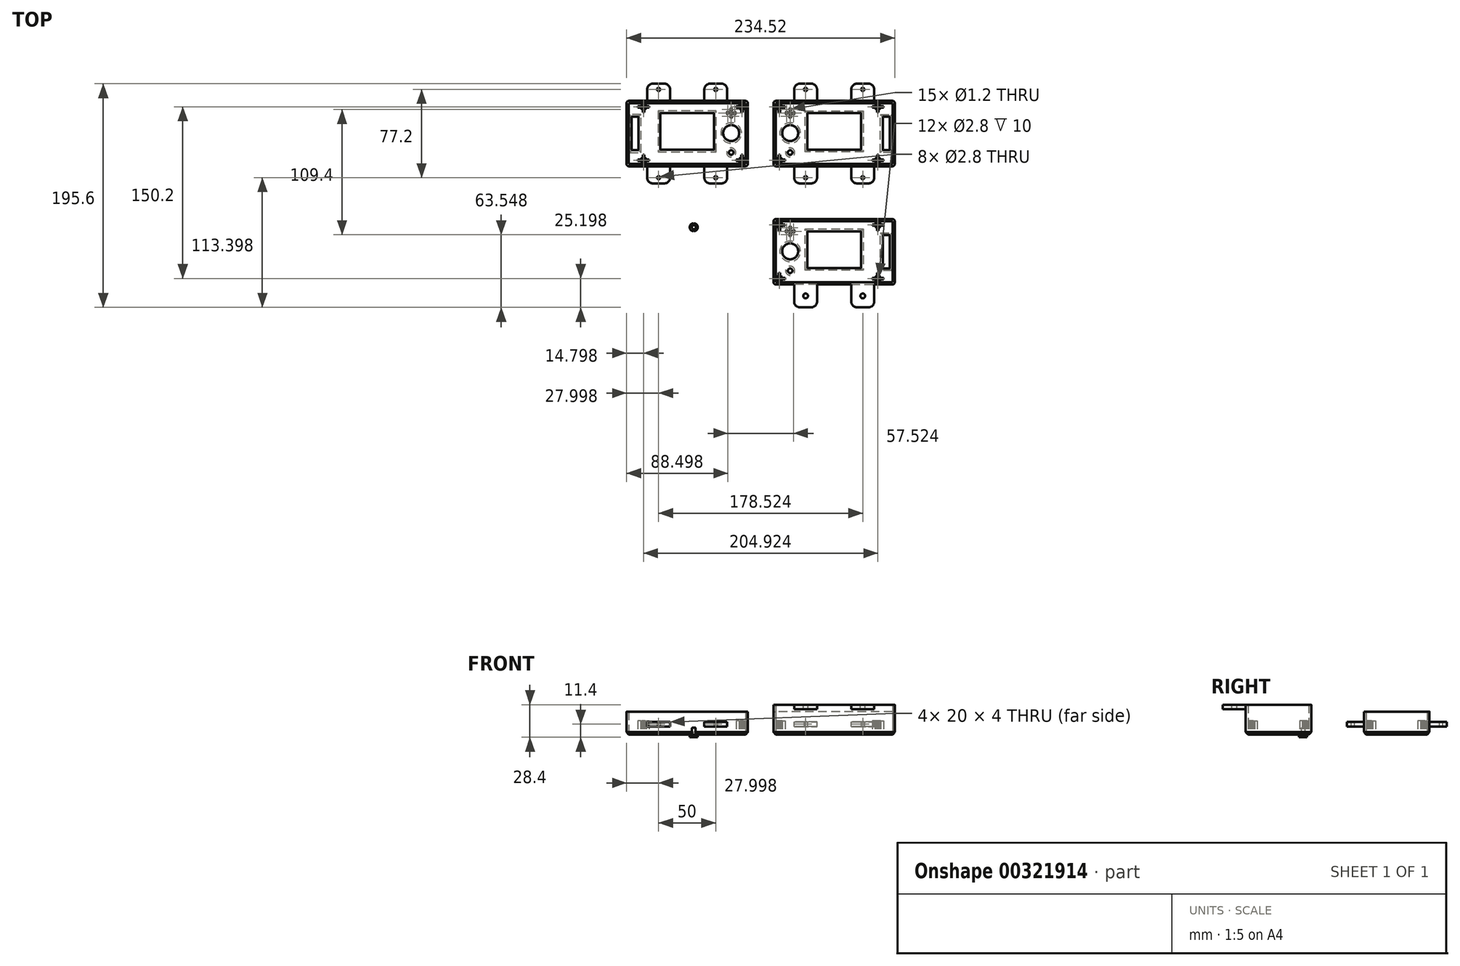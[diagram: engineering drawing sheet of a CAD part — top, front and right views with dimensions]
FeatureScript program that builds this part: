
annotation { "Feature Type Name" : "Feature", "Feature Type Description" : "" }
export const myFeature = defineFeature(function(context is Context, id is Id, definition is map)
    precondition{}
    {
        {
            var Q0;
            Q0=qCreatedBy(makeId("Top.planeOp"),FACE);
            var sketch = newSketch(context, id + "F0", { "sketchPlane" : qUnion([Q0])});
            skLineSegment(sketch, "E0.bottom", {"start": v(-115.26, 57.83) * mm, "end": v(-13.26, 57.83) * mm});
            skLineSegment(sketch, "E0.top", {"start": v(-115.26, 4.63) * mm, "end": v(-13.26, 4.63) * mm});
            skLineSegment(sketch, "E0.left", {"start": v(-115.26, 57.83) * mm, "end": v(-115.26, 4.63) * mm});
            skLineSegment(sketch, "E0.right", {"start": v(-13.26, 57.83) * mm, "end": v(-13.26, 4.63) * mm});
            skLineSegment(sketch, "E1.bottom", {"start": v(-117.26, 59.83) * mm, "end": v(-11.26, 59.83) * mm});
            skLineSegment(sketch, "E1.top", {"start": v(-117.26, 2.63) * mm, "end": v(-11.26, 2.63) * mm});
            skLineSegment(sketch, "E1.left", {"start": v(-117.26, 59.83) * mm, "end": v(-117.26, 2.63) * mm});
            skLineSegment(sketch, "E1.right", {"start": v(-11.26, 59.83) * mm, "end": v(-11.26, 2.63) * mm});
            skLineSegment(sketch, "E2.bottom", {"start": v(-87.76, 49.13) * mm, "end": v(-40.76, 49.13) * mm});
            skLineSegment(sketch, "E2.top", {"start": v(-87.76, 17.13) * mm, "end": v(-40.76, 17.13) * mm});
            skLineSegment(sketch, "E2.left", {"start": v(-87.76, 49.13) * mm, "end": v(-87.76, 17.13) * mm});
            skLineSegment(sketch, "E2.right", {"start": v(-40.76, 49.13) * mm, "end": v(-40.76, 17.13) * mm});
            skCircle(sketch, "E3", {"center": v(-25.76, 31.63) * mm, "radius": 7 * mm});
            skCircle(sketch, "E4", {"center": v(-25.76, 14.63) * mm, "radius": 2 * mm});
            skLineSegment(sketch, "E5.bottom", {"start": v(-112.76, 45.83) * mm, "end": v(-106.76, 45.83) * mm});
            skLineSegment(sketch, "E5.top", {"start": v(-112.76, 16.63) * mm, "end": v(-106.76, 16.63) * mm});
            skLineSegment(sketch, "E5.left", {"start": v(-112.76, 45.83) * mm, "end": v(-112.76, 16.63) * mm});
            skLineSegment(sketch, "E5.right", {"start": v(-106.76, 45.83) * mm, "end": v(-106.76, 16.63) * mm});
            skCircle(sketch, "E6", {"center": v(-25.76, 49.18) * mm, "radius": 0.6 * mm});
            skCircle(sketch, "E7", {"center": v(-28.76, 49.18) * mm, "radius": 0.6 * mm});
            skCircle(sketch, "E8", {"center": v(-25.76, 46.18) * mm, "radius": 0.6 * mm});
            skCircle(sketch, "E9", {"center": v(-22.76, 49.18) * mm, "radius": 0.6 * mm});
            skCircle(sketch, "E10", {"center": v(-25.76, 52.18) * mm, "radius": 0.6 * mm});
            skSolve(sketch);
        }
        {
            var Q0;
            Q0=makeQuery(id+"F0.imprint","IMPRINT",FACE,{"disambiguationData":[TD([[makeQuery(id+"F0.imprint","IMPRINT",EDGE,{"derivedFrom":sQuery(id+"F0.wireOp",EDGE,"E0.bottom")}),-1.0]])]});
            extrude(context, id + "F1", {"entities" : qUnion([Q0]), "depth" : 2 * mm, "offsetDistance" : 25 * mm});
        }
        {
            var Q0;
            Q0=makeQuery(id+"F0.imprint","IMPRINT",FACE,{"disambiguationData":[TD([[makeQuery(id+"F0.imprint","IMPRINT",EDGE,{"derivedFrom":sQuery(id+"F0.wireOp",EDGE,"E0.bottom")}),1.0]])]});
            extrude(context, id + "F2", {"entities" : qUnion([Q0]), "operationType" : NewBodyOperationType.ADD, "depth" : 20 * mm, "offsetDistance" : 25 * mm});
        }
        {
            var Q0;
            Q0=makeQuery(id+"F1.opExtrude","CAP_FACE",FACE,{"disambiguationData":[OSD([sQuery(id+"F0.wireOp",EDGE,"E0.bottom"),sQuery(id+"F0.wireOp",EDGE,"E0.top"),sQuery(id+"F0.wireOp",EDGE,"E0.left"),sQuery(id+"F0.wireOp",EDGE,"E0.right"),sQuery(id+"F0.wireOp",EDGE,"E2.bottom"),sQuery(id+"F0.wireOp",EDGE,"E2.top"),sQuery(id+"F0.wireOp",EDGE,"E2.left"),sQuery(id+"F0.wireOp",EDGE,"E2.right"),sQuery(id+"F0.wireOp",EDGE,"E3"),sQuery(id+"F0.wireOp",EDGE,"E4")])],"isStart":false});
            var sketch = newSketch(context, id + "F3", { "sketchPlane" : qUnion([Q0])});
            skCircle(sketch, "E11", {"center": v(-16.46, 54.63) * mm, "radius": 1.4 * mm});
            skCircle(sketch, "E12", {"center": v(-16.46, 7.83) * mm, "radius": 1.4 * mm});
            skCircle(sketch, "E13", {"center": v(-102.46, 54.63) * mm, "radius": 1.4 * mm});
            skCircle(sketch, "E14", {"center": v(-102.46, 7.83) * mm, "radius": 1.4 * mm});
            skCircle(sketch, "E15", {"center": v(-16.46, 54.63) * mm, "radius": 2.6 * mm});
            skCircle(sketch, "E16", {"center": v(-16.46, 7.83) * mm, "radius": 2.6 * mm});
            skCircle(sketch, "E17", {"center": v(-102.46, 7.83) * mm, "radius": 2.6 * mm});
            skCircle(sketch, "E18", {"center": v(-102.46, 54.63) * mm, "radius": 2.6 * mm});
            skLineSegment(sketch, "E19.top", {"start": v(-17.06, 49.7) * mm, "end": v(-15.86, 49.7) * mm});
            skLineSegment(sketch, "E19.left", {"start": v(-17.06, 52.1) * mm, "end": v(-17.06, 49.7) * mm});
            skLineSegment(sketch, "E19.right", {"start": v(-15.86, 52.1) * mm, "end": v(-15.86, 49.7) * mm});
            skLineSegment(sketch, "E20.bottom", {"start": v(-19, 55.23) * mm, "end": v(-21.4, 55.23) * mm});
            skLineSegment(sketch, "E20.top", {"start": v(-19, 54.03) * mm, "end": v(-21.4, 54.03) * mm});
            skLineSegment(sketch, "E20.right", {"start": v(-21.4, 55.23) * mm, "end": v(-21.4, 54.03) * mm});
            skLineSegment(sketch, "E21.top", {"start": v(-17.06, 57.83) * mm, "end": v(-15.86, 57.83) * mm});
            skLineSegment(sketch, "E21.left", {"start": v(-17.06, 57.16) * mm, "end": v(-17.06, 57.83) * mm});
            skLineSegment(sketch, "E21.right", {"start": v(-15.86, 57.16) * mm, "end": v(-15.86, 57.83) * mm});
            skLineSegment(sketch, "E22.bottom", {"start": v(-13.93, 55.23) * mm, "end": v(-13.26, 55.23) * mm});
            skLineSegment(sketch, "E22.top", {"start": v(-13.93, 54.03) * mm, "end": v(-13.26, 54.03) * mm});
            skLineSegment(sketch, "E22.right", {"start": v(-13.26, 55.23) * mm, "end": v(-13.26, 54.03) * mm});
            skLineSegment(sketch, "E23.top", {"start": v(-17.06, 12.76) * mm, "end": v(-15.86, 12.76) * mm});
            skLineSegment(sketch, "E23.left", {"start": v(-17.06, 10.36) * mm, "end": v(-17.06, 12.76) * mm});
            skLineSegment(sketch, "E23.right", {"start": v(-15.86, 10.36) * mm, "end": v(-15.86, 12.76) * mm});
            skLineSegment(sketch, "E24.bottom", {"start": v(-19, 8.43) * mm, "end": v(-21.4, 8.43) * mm});
            skLineSegment(sketch, "E24.top", {"start": v(-19, 7.23) * mm, "end": v(-21.4, 7.23) * mm});
            skLineSegment(sketch, "E24.right", {"start": v(-21.4, 8.43) * mm, "end": v(-21.4, 7.23) * mm});
            skLineSegment(sketch, "E25.top", {"start": v(-17.06, 4.63) * mm, "end": v(-15.86, 4.63) * mm});
            skLineSegment(sketch, "E25.left", {"start": v(-17.06, 5.3) * mm, "end": v(-17.06, 4.63) * mm});
            skLineSegment(sketch, "E25.right", {"start": v(-15.86, 5.3) * mm, "end": v(-15.86, 4.63) * mm});
            skLineSegment(sketch, "E26.bottom", {"start": v(-13.93, 7.23) * mm, "end": v(-13.26, 7.23) * mm});
            skLineSegment(sketch, "E26.top", {"start": v(-13.93, 8.43) * mm, "end": v(-13.26, 8.43) * mm});
            skLineSegment(sketch, "E26.right", {"start": v(-13.26, 7.23) * mm, "end": v(-13.26, 8.43) * mm});
            skLineSegment(sketch, "E27.bottom", {"start": v(-105, 55.23) * mm, "end": v(-107.4, 55.23) * mm});
            skLineSegment(sketch, "E27.top", {"start": v(-105, 54.03) * mm, "end": v(-107.4, 54.03) * mm});
            skLineSegment(sketch, "E27.right", {"start": v(-107.4, 55.23) * mm, "end": v(-107.4, 54.03) * mm});
            skLineSegment(sketch, "E28.bottom", {"start": v(-99.93, 55.23) * mm, "end": v(-97.53, 55.23) * mm});
            skLineSegment(sketch, "E28.top", {"start": v(-99.93, 54.03) * mm, "end": v(-97.53, 54.03) * mm});
            skLineSegment(sketch, "E28.right", {"start": v(-97.53, 55.23) * mm, "end": v(-97.53, 54.03) * mm});
            skLineSegment(sketch, "E29.top", {"start": v(-103.06, 49.7) * mm, "end": v(-101.86, 49.7) * mm});
            skLineSegment(sketch, "E29.left", {"start": v(-103.06, 52.1) * mm, "end": v(-103.06, 49.7) * mm});
            skLineSegment(sketch, "E29.right", {"start": v(-101.86, 52.1) * mm, "end": v(-101.86, 49.7) * mm});
            skLineSegment(sketch, "E30.top", {"start": v(-103.06, 57.83) * mm, "end": v(-101.86, 57.83) * mm});
            skLineSegment(sketch, "E30.left", {"start": v(-103.06, 57.16) * mm, "end": v(-103.06, 57.83) * mm});
            skLineSegment(sketch, "E30.right", {"start": v(-101.86, 57.16) * mm, "end": v(-101.86, 57.83) * mm});
            skLineSegment(sketch, "E31.top", {"start": v(-103.06, 12.76) * mm, "end": v(-101.86, 12.76) * mm});
            skLineSegment(sketch, "E31.left", {"start": v(-103.06, 10.36) * mm, "end": v(-103.06, 12.76) * mm});
            skLineSegment(sketch, "E31.right", {"start": v(-101.86, 10.36) * mm, "end": v(-101.86, 12.76) * mm});
            skLineSegment(sketch, "E32.bottom", {"start": v(-105, 8.43) * mm, "end": v(-107.4, 8.43) * mm});
            skLineSegment(sketch, "E32.top", {"start": v(-105, 7.23) * mm, "end": v(-107.4, 7.23) * mm});
            skLineSegment(sketch, "E32.right", {"start": v(-107.4, 8.43) * mm, "end": v(-107.4, 7.23) * mm});
            skLineSegment(sketch, "E33.bottom", {"start": v(-99.93, 8.43) * mm, "end": v(-97.53, 8.43) * mm});
            skLineSegment(sketch, "E33.top", {"start": v(-99.93, 7.23) * mm, "end": v(-97.53, 7.23) * mm});
            skLineSegment(sketch, "E33.right", {"start": v(-97.53, 8.43) * mm, "end": v(-97.53, 7.23) * mm});
            skLineSegment(sketch, "E34.top", {"start": v(-103.06, 4.63) * mm, "end": v(-101.86, 4.63) * mm});
            skLineSegment(sketch, "E34.left", {"start": v(-103.06, 5.3) * mm, "end": v(-103.06, 4.63) * mm});
            skLineSegment(sketch, "E34.right", {"start": v(-101.86, 5.3) * mm, "end": v(-101.86, 4.63) * mm});
            skLineSegment(sketch, "E35.bottom", {"start": v(-88.96, 50.33) * mm, "end": v(-39.56, 50.33) * mm});
            skLineSegment(sketch, "E35.top", {"start": v(-88.96, 15.93) * mm, "end": v(-39.56, 15.93) * mm});
            skLineSegment(sketch, "E35.left", {"start": v(-88.96, 50.33) * mm, "end": v(-88.96, 15.93) * mm});
            skLineSegment(sketch, "E35.right", {"start": v(-39.56, 50.33) * mm, "end": v(-39.56, 15.93) * mm});
            skSolve(sketch);
        }
        {
            var Q0;
            Q0=makeQuery(id+"F3.imprint","IMPRINT",FACE,{"disambiguationData":[TD([[makeQuery(id+"F3.imprint","IMPRINT",EDGE,{"derivedFrom":sQuery(id+"F3.wireOp",EDGE,"E14")}),-1.0]])]});
            var Q1;
            Q1=makeQuery(id+"F3.imprint","IMPRINT",FACE,{"disambiguationData":[TD([[makeQuery(id+"F3.imprint","IMPRINT",EDGE,{"derivedFrom":sQuery(id+"F3.wireOp",EDGE,"E31.top")}),-1.0]])]});
            var Q2;
            {var subQ0=sQuery(id+"F3.wireOp",EDGE,"E32.bottom");Q2=makeQuery(id+"F3.imprint","IMPRINT",FACE,{"disambiguationData":[TD([[makeQuery(id+"F3.imprint","IMPRINT",EDGE,{"derivedFrom":subQ0}),1.0]])]});}
            var Q3;
            Q3=makeQuery(id+"F3.imprint","IMPRINT",FACE,{"disambiguationData":[TD([[makeQuery(id+"F3.imprint","IMPRINT",EDGE,{"derivedFrom":sQuery(id+"F3.wireOp",EDGE,"E34.top")}),1.0]])]});
            var Q4;
            {var subQ0=sQuery(id+"F3.wireOp",EDGE,"E33.bottom");Q4=makeQuery(id+"F3.imprint","IMPRINT",FACE,{"disambiguationData":[TD([[makeQuery(id+"F3.imprint","IMPRINT",EDGE,{"derivedFrom":subQ0}),-1.0]])]});}
            var Q5;
            {var subQ0=sQuery(id+"F3.wireOp",EDGE,"E24.bottom");Q5=makeQuery(id+"F3.imprint","IMPRINT",FACE,{"disambiguationData":[TD([[makeQuery(id+"F3.imprint","IMPRINT",EDGE,{"derivedFrom":subQ0}),1.0]])]});}
            var Q6;
            Q6=makeQuery(id+"F3.imprint","IMPRINT",FACE,{"disambiguationData":[TD([[makeQuery(id+"F3.imprint","IMPRINT",EDGE,{"derivedFrom":sQuery(id+"F3.wireOp",EDGE,"E12")}),-1.0]])]});
            var Q7;
            Q7=makeQuery(id+"F3.imprint","IMPRINT",FACE,{"disambiguationData":[TD([[makeQuery(id+"F3.imprint","IMPRINT",EDGE,{"derivedFrom":sQuery(id+"F3.wireOp",EDGE,"E25.top")}),1.0]])]});
            var Q8;
            {var subQ0=sQuery(id+"F3.wireOp",EDGE,"E26.bottom");Q8=makeQuery(id+"F3.imprint","IMPRINT",FACE,{"disambiguationData":[TD([[makeQuery(id+"F3.imprint","IMPRINT",EDGE,{"derivedFrom":subQ0}),1.0]])]});}
            var Q9;
            Q9=makeQuery(id+"F3.imprint","IMPRINT",FACE,{"disambiguationData":[TD([[makeQuery(id+"F3.imprint","IMPRINT",EDGE,{"derivedFrom":sQuery(id+"F3.wireOp",EDGE,"E23.top")}),-1.0]])]});
            var Q10;
            Q10=makeQuery(id+"F3.imprint","IMPRINT",FACE,{"disambiguationData":[TD([[makeQuery(id+"F3.imprint","IMPRINT",EDGE,{"derivedFrom":sQuery(id+"F3.wireOp",EDGE,"E11")}),-1.0]])]});
            var Q11;
            {var subQ0=sQuery(id+"F3.wireOp",EDGE,"E22.bottom");Q11=makeQuery(id+"F3.imprint","IMPRINT",FACE,{"disambiguationData":[TD([[makeQuery(id+"F3.imprint","IMPRINT",EDGE,{"derivedFrom":subQ0}),-1.0]])]});}
            var Q12;
            Q12=makeQuery(id+"F3.imprint","IMPRINT",FACE,{"disambiguationData":[TD([[makeQuery(id+"F3.imprint","IMPRINT",EDGE,{"derivedFrom":sQuery(id+"F3.wireOp",EDGE,"E21.top")}),-1.0]])]});
            var Q13;
            {var subQ0=sQuery(id+"F3.wireOp",EDGE,"E20.bottom");Q13=makeQuery(id+"F3.imprint","IMPRINT",FACE,{"disambiguationData":[TD([[makeQuery(id+"F3.imprint","IMPRINT",EDGE,{"derivedFrom":subQ0}),1.0]])]});}
            var Q14;
            Q14=makeQuery(id+"F3.imprint","IMPRINT",FACE,{"disambiguationData":[TD([[makeQuery(id+"F3.imprint","IMPRINT",EDGE,{"derivedFrom":sQuery(id+"F3.wireOp",EDGE,"E19.top")}),1.0]])]});
            var Q15;
            Q15=makeQuery(id+"F3.imprint","IMPRINT",FACE,{"disambiguationData":[TD([[makeQuery(id+"F3.imprint","IMPRINT",EDGE,{"derivedFrom":sQuery(id+"F3.wireOp",EDGE,"E13")}),-1.0]])]});
            var Q16;
            {var subQ0=sQuery(id+"F3.wireOp",EDGE,"E27.bottom");Q16=makeQuery(id+"F3.imprint","IMPRINT",FACE,{"disambiguationData":[TD([[makeQuery(id+"F3.imprint","IMPRINT",EDGE,{"derivedFrom":subQ0}),1.0]])]});}
            var Q17;
            Q17=makeQuery(id+"F3.imprint","IMPRINT",FACE,{"disambiguationData":[TD([[makeQuery(id+"F3.imprint","IMPRINT",EDGE,{"derivedFrom":sQuery(id+"F3.wireOp",EDGE,"E29.top")}),1.0]])]});
            var Q18;
            {var subQ0=sQuery(id+"F3.wireOp",EDGE,"E28.bottom");Q18=makeQuery(id+"F3.imprint","IMPRINT",FACE,{"disambiguationData":[TD([[makeQuery(id+"F3.imprint","IMPRINT",EDGE,{"derivedFrom":subQ0}),-1.0]])]});}
            var Q19;
            Q19=makeQuery(id+"F3.imprint","IMPRINT",FACE,{"disambiguationData":[TD([[makeQuery(id+"F3.imprint","IMPRINT",EDGE,{"derivedFrom":sQuery(id+"F3.wireOp",EDGE,"E30.top")}),-1.0]])]});
            extrude(context, id + "F4", {"entities" : qUnion([Q0, Q1, Q2, Q3, Q4, Q5, Q6, Q7, Q8, Q9, Q10, Q11, Q12, Q13, Q14, Q15, Q16, Q17, Q18, Q19]), "operationType" : NewBodyOperationType.ADD, "depth" : 10 * mm, "offsetDistance" : 25 * mm});
        }
        {
            var Q0;
            Q0=makeQuery(id+"F2.opExtrude","SWEPT_EDGE",EDGE,{"disambiguationData":[OSD([sQuery(id+"F0.wireOp",EDGE,"E1.bottom"),sQuery(id+"F0.wireOp",EDGE,"E1.left")])]});
            var Q1;
            Q1=makeQuery(id+"F2.opExtrude","SWEPT_EDGE",EDGE,{"disambiguationData":[OSD([sQuery(id+"F0.wireOp",EDGE,"E1.top"),sQuery(id+"F0.wireOp",EDGE,"E1.left")])]});
            var Q2;
            Q2=makeQuery(id+"F2.opExtrude","SWEPT_EDGE",EDGE,{"disambiguationData":[OSD([sQuery(id+"F0.wireOp",EDGE,"E1.bottom"),sQuery(id+"F0.wireOp",EDGE,"E1.right")])]});
            var Q3;
            Q3=makeQuery(id+"F2.opExtrude","SWEPT_EDGE",EDGE,{"disambiguationData":[OSD([sQuery(id+"F0.wireOp",EDGE,"E1.top"),sQuery(id+"F0.wireOp",EDGE,"E1.right")])]});
            fillet(context, id + "F5", {"entities" : qUnion([Q0, Q1, Q2, Q3]), "radius" : 2 * mm, "tangentPropagation" : true, "allowEdgeOverflow" : false});
        }
        {
            var Q0;
            Q0=makeQuery(id+"F1.opExtrude","CAP_EDGE",EDGE,{"disambiguationData":[OSD([sQuery(id+"F0.wireOp",EDGE,"E6")])],"isStart":true});
            var Q1;
            Q1=makeQuery(id+"F1.opExtrude","CAP_EDGE",EDGE,{"disambiguationData":[OSD([sQuery(id+"F0.wireOp",EDGE,"E10")])],"isStart":true});
            var Q2;
            Q2=makeQuery(id+"F1.opExtrude","CAP_EDGE",EDGE,{"disambiguationData":[OSD([sQuery(id+"F0.wireOp",EDGE,"E9")])],"isStart":true});
            var Q3;
            Q3=makeQuery(id+"F1.opExtrude","CAP_EDGE",EDGE,{"disambiguationData":[OSD([sQuery(id+"F0.wireOp",EDGE,"E8")])],"isStart":true});
            var Q4;
            Q4=makeQuery(id+"F1.opExtrude","CAP_EDGE",EDGE,{"disambiguationData":[OSD([sQuery(id+"F0.wireOp",EDGE,"E7")])],"isStart":true});
            chamfer(context, id + "F6", {"entities" : qUnion([Q0, Q1, Q2, Q3, Q4]), "width" : 1 * mm, "tangentPropagation" : true});
        }
        {
            var Q0;
            Q0=makeQuery(id+"F1.opExtrude","CAP_EDGE",EDGE,{"disambiguationData":[OSD([sQuery(id+"F0.wireOp",EDGE,"E3")])],"isStart":true});
            var Q1;
            Q1=makeQuery(id+"F1.opExtrude","CAP_EDGE",EDGE,{"disambiguationData":[OSD([sQuery(id+"F0.wireOp",EDGE,"E4")])],"isStart":true});
            var Q2;
            Q2=makeQuery(id+"F2.opExtrude","CAP_EDGE",EDGE,{"disambiguationData":[OSD([sQuery(id+"F0.wireOp",EDGE,"E1.top")])],"isStart":true});
            var Q3;
            Q3=makeQuery(id+"F2.opExtrude","CAP_EDGE",EDGE,{"disambiguationData":[OSD([sQuery(id+"F0.wireOp",EDGE,"E1.right")])],"isStart":true});
            var Q4;
            Q4=makeQuery(id+"F2.opExtrude","CAP_EDGE",EDGE,{"disambiguationData":[OSD([sQuery(id+"F0.wireOp",EDGE,"E1.bottom")])],"isStart":true});
            var Q5;
            Q5=makeQuery(id+"F2.opExtrude","CAP_EDGE",EDGE,{"disambiguationData":[OSD([sQuery(id+"F0.wireOp",EDGE,"E1.left")])],"isStart":true});
            var Q6;
            Q6=makeQuery(id+"F1.opExtrude","CAP_EDGE",EDGE,{"disambiguationData":[OSD([sQuery(id+"F0.wireOp",EDGE,"E2.right")])],"isStart":true});
            var Q7;
            Q7=makeQuery(id+"F1.opExtrude","CAP_EDGE",EDGE,{"disambiguationData":[OSD([sQuery(id+"F0.wireOp",EDGE,"E2.bottom")])],"isStart":true});
            var Q8;
            Q8=makeQuery(id+"F1.opExtrude","CAP_EDGE",EDGE,{"disambiguationData":[OSD([sQuery(id+"F0.wireOp",EDGE,"E2.left")])],"isStart":true});
            var Q9;
            Q9=makeQuery(id+"F1.opExtrude","CAP_EDGE",EDGE,{"disambiguationData":[OSD([sQuery(id+"F0.wireOp",EDGE,"E2.top")])],"isStart":true});
            var Q10;
            Q10=makeQuery(id+"F1.opExtrude","CAP_EDGE",EDGE,{"disambiguationData":[OSD([sQuery(id+"F0.wireOp",EDGE,"E5.right")])],"isStart":true});
            var Q11;
            Q11=makeQuery(id+"F1.opExtrude","CAP_EDGE",EDGE,{"disambiguationData":[OSD([sQuery(id+"F0.wireOp",EDGE,"E5.left")])],"isStart":true});
            var Q12;
            Q12=makeQuery(id+"F1.opExtrude","CAP_EDGE",EDGE,{"disambiguationData":[OSD([sQuery(id+"F0.wireOp",EDGE,"E5.bottom")])],"isStart":true});
            var Q13;
            Q13=makeQuery(id+"F1.opExtrude","CAP_EDGE",EDGE,{"disambiguationData":[OSD([sQuery(id+"F0.wireOp",EDGE,"E5.top")])],"isStart":true});
            chamfer(context, id + "F7", {"entities" : qUnion([Q0, Q1, Q2, Q3, Q4, Q5, Q6, Q7, Q8, Q9, Q10, Q11, Q12, Q13]), "width" : 2 * mm, "tangentPropagation" : true});
        }
        {
            var Q0;
            Q0=makeQuery(id+"F2.opExtrude","SWEPT_FACE",FACE,{"disambiguationData":[OSD([sQuery(id+"F0.wireOp",EDGE,"E1.bottom")])]});
            var sketch = newSketch(context, id + "F8", { "sketchPlane" : qUnion([Q0])});
            skLineSegment(sketch, "E36.bottom", {"start": v(99.26, 7) * mm, "end": v(79.26, 7) * mm});
            skLineSegment(sketch, "E36.top", {"start": v(99.26, 11) * mm, "end": v(79.26, 11) * mm});
            skLineSegment(sketch, "E36.left", {"start": v(99.26, 7) * mm, "end": v(99.26, 11) * mm});
            skLineSegment(sketch, "E36.right", {"start": v(79.26, 7) * mm, "end": v(79.26, 11) * mm});
            skLineSegment(sketch, "E37.bottom", {"start": v(49.26, 7) * mm, "end": v(29.26, 7) * mm});
            skLineSegment(sketch, "E37.top", {"start": v(49.26, 11) * mm, "end": v(29.26, 11) * mm});
            skLineSegment(sketch, "E37.left", {"start": v(49.26, 7) * mm, "end": v(49.26, 11) * mm});
            skLineSegment(sketch, "E37.right", {"start": v(29.26, 7) * mm, "end": v(29.26, 11) * mm});
            skSolve(sketch);
        }
        {
            var Q0;
            Q0=makeQuery(id+"F2.opExtrude","SWEPT_FACE",FACE,{"disambiguationData":[OSD([sQuery(id+"F0.wireOp",EDGE,"E1.top")])]});
            var sketch = newSketch(context, id + "F9", { "sketchPlane" : qUnion([Q0])});
            skLineSegment(sketch, "E38.bottom", {"start": v(-29.26, 7) * mm, "end": v(-49.26, 7) * mm});
            skLineSegment(sketch, "E38.top", {"start": v(-29.26, 11) * mm, "end": v(-49.26, 11) * mm});
            skLineSegment(sketch, "E38.left", {"start": v(-29.26, 7) * mm, "end": v(-29.26, 11) * mm});
            skLineSegment(sketch, "E38.right", {"start": v(-49.26, 7) * mm, "end": v(-49.26, 11) * mm});
            skLineSegment(sketch, "E39.bottom", {"start": v(-79.26, 7) * mm, "end": v(-99.26, 7) * mm});
            skLineSegment(sketch, "E39.top", {"start": v(-79.26, 11) * mm, "end": v(-99.26, 11) * mm});
            skLineSegment(sketch, "E39.left", {"start": v(-79.26, 7) * mm, "end": v(-79.26, 11) * mm});
            skLineSegment(sketch, "E39.right", {"start": v(-99.26, 7) * mm, "end": v(-99.26, 11) * mm});
            skSolve(sketch);
        }
        {
            var Q0;
            Q0=makeQuery(id+"F9.imprint","IMPRINT",FACE,{"disambiguationData":[TD([[makeQuery(id+"F9.imprint","IMPRINT",EDGE,{"derivedFrom":sQuery(id+"F9.wireOp",EDGE,"E39.bottom")}),-1.0]])]});
            var Q1;
            Q1=makeQuery(id+"F9.imprint","IMPRINT",FACE,{"disambiguationData":[TD([[makeQuery(id+"F9.imprint","IMPRINT",EDGE,{"derivedFrom":sQuery(id+"F9.wireOp",EDGE,"E38.bottom")}),-1.0]])]});
            extrude(context, id + "F10", {"entities" : qUnion([Q0, Q1]), "operationType" : NewBodyOperationType.ADD, "depth" : 15 * mm, "offsetDistance" : 25 * mm});
        }
        {
            var Q0;
            Q0=makeQuery(id+"F8.imprint","IMPRINT",FACE,{"disambiguationData":[TD([[makeQuery(id+"F8.imprint","IMPRINT",EDGE,{"derivedFrom":sQuery(id+"F8.wireOp",EDGE,"E36.bottom")}),-1.0]])]});
            var Q1;
            Q1=makeQuery(id+"F8.imprint","IMPRINT",FACE,{"disambiguationData":[TD([[makeQuery(id+"F8.imprint","IMPRINT",EDGE,{"derivedFrom":sQuery(id+"F8.wireOp",EDGE,"E37.bottom")}),-1.0]])]});
            extrude(context, id + "F11", {"entities" : qUnion([Q0, Q1]), "operationType" : NewBodyOperationType.ADD, "depth" : 15 * mm, "offsetDistance" : 25 * mm});
        }
        {
            var Q0;
            Q0=makeQuery(id+"F10.opExtrude","CAP_EDGE",EDGE,{"disambiguationData":[OSD([sQuery(id+"F9.wireOp",EDGE,"E39.right")])],"isStart":false});
            var Q1;
            Q1=makeQuery(id+"F10.opExtrude","CAP_EDGE",EDGE,{"disambiguationData":[OSD([sQuery(id+"F9.wireOp",EDGE,"E39.left")])],"isStart":false});
            var Q2;
            Q2=makeQuery(id+"F10.opExtrude","CAP_EDGE",EDGE,{"disambiguationData":[OSD([sQuery(id+"F9.wireOp",EDGE,"E38.right")])],"isStart":false});
            var Q3;
            Q3=makeQuery(id+"F10.opExtrude","CAP_EDGE",EDGE,{"disambiguationData":[OSD([sQuery(id+"F9.wireOp",EDGE,"E38.left")])],"isStart":false});
            var Q4;
            Q4=makeQuery(id+"F11.opExtrude","CAP_EDGE",EDGE,{"disambiguationData":[OSD([sQuery(id+"F8.wireOp",EDGE,"E37.right")])],"isStart":false});
            var Q5;
            Q5=makeQuery(id+"F11.opExtrude","CAP_EDGE",EDGE,{"disambiguationData":[OSD([sQuery(id+"F8.wireOp",EDGE,"E36.right")])],"isStart":false});
            var Q6;
            Q6=makeQuery(id+"F11.opExtrude","CAP_EDGE",EDGE,{"disambiguationData":[OSD([sQuery(id+"F8.wireOp",EDGE,"E37.left")])],"isStart":false});
            var Q7;
            Q7=makeQuery(id+"F11.opExtrude","CAP_EDGE",EDGE,{"disambiguationData":[OSD([sQuery(id+"F8.wireOp",EDGE,"E36.left")])],"isStart":false});
            fillet(context, id + "F12", {"entities" : qUnion([Q0, Q1, Q2, Q3, Q4, Q5, Q6, Q7]), "radius" : 5 * mm, "tangentPropagation" : true, "allowEdgeOverflow" : false});
        }
        {
            var Q0;
            Q0=makeQuery(id+"F10.opExtrude","SWEPT_FACE",FACE,{"disambiguationData":[OSD([sQuery(id+"F9.wireOp",EDGE,"E39.bottom")])]});
            var sketch = newSketch(context, id + "F13", { "sketchPlane" : qUnion([Q0])});
            skCircle(sketch, "E40", {"center": v(-89.26, 7.37) * mm, "radius": 1.4 * mm});
            skPoint(sketch, "E40.centerSnap0", {"position": v(-79.01, 7.37) * mm});
            skPoint(sketch, "E40.centerSnap1", {"position": v(-89.26, 12.37) * mm});
            skCircle(sketch, "E41", {"center": v(-39.26, 7.37) * mm, "radius": 1.4 * mm});
            skCircle(sketch, "E42", {"center": v(-89.26, -69.83) * mm, "radius": 1.4 * mm});
            skCircle(sketch, "E43", {"center": v(-39.26, -69.83) * mm, "radius": 1.4 * mm});
            skSolve(sketch);
        }
        {
            var Q0;
            Q0=makeQuery(id+"F13.imprint","IMPRINT",FACE,{"disambiguationData":[TD([[makeQuery(id+"F13.imprint","IMPRINT",EDGE,{"derivedFrom":sQuery(id+"F13.wireOp",EDGE,"E40")}),1.0]])]});
            var Q1;
            Q1=makeQuery(id+"F13.imprint","IMPRINT",FACE,{"disambiguationData":[TD([[makeQuery(id+"F13.imprint","IMPRINT",EDGE,{"derivedFrom":sQuery(id+"F13.wireOp",EDGE,"E41")}),1.0]])]});
            var Q2;
            Q2=makeQuery(id+"F13.imprint","IMPRINT",FACE,{"disambiguationData":[TD([[makeQuery(id+"F13.imprint","IMPRINT",EDGE,{"derivedFrom":sQuery(id+"F13.wireOp",EDGE,"E43")}),1.0]])]});
            var Q3;
            Q3=makeQuery(id+"F13.imprint","IMPRINT",FACE,{"disambiguationData":[TD([[makeQuery(id+"F13.imprint","IMPRINT",EDGE,{"derivedFrom":sQuery(id+"F13.wireOp",EDGE,"E42")}),1.0]])]});
            extrude(context, id + "F14", {"entities" : qUnion([Q0, Q1, Q2, Q3]), "operationType" : NewBodyOperationType.REMOVE, "oppositeDirection" : true, "depth" : 25 * mm, "offsetDistance" : 25 * mm});
        }
        {
            var Q0;
            Q0=makeQuery(id+"F1.opExtrude","SWEPT_BODY",BODY,{"disambiguationData":[OSD([sQuery(id+"F0.wireOp",EDGE,"E0.bottom"),sQuery(id+"F0.wireOp",EDGE,"E0.top"),sQuery(id+"F0.wireOp",EDGE,"E0.left"),sQuery(id+"F0.wireOp",EDGE,"E0.right"),sQuery(id+"F0.wireOp",EDGE,"E2.bottom"),sQuery(id+"F0.wireOp",EDGE,"E2.top"),sQuery(id+"F0.wireOp",EDGE,"E2.left"),sQuery(id+"F0.wireOp",EDGE,"E2.right"),sQuery(id+"F0.wireOp",EDGE,"E3"),sQuery(id+"F0.wireOp",EDGE,"E4"),sQuery(id+"F0.wireOp",EDGE,"E5.bottom"),sQuery(id+"F0.wireOp",EDGE,"E5.top"),sQuery(id+"F0.wireOp",EDGE,"E5.left"),sQuery(id+"F0.wireOp",EDGE,"E5.right"),sQuery(id+"F0.wireOp",EDGE,"E6"),sQuery(id+"F0.wireOp",EDGE,"E7"),sQuery(id+"F0.wireOp",EDGE,"E8"),sQuery(id+"F0.wireOp",EDGE,"E9"),sQuery(id+"F0.wireOp",EDGE,"E10")])]});
            var Q1;
            Q1=qCreatedBy(makeId("Right.planeOp"),FACE);
            mirror(context, id + "F15", {"entities" : qUnion([Q0]), "mirrorPlane" : qUnion([Q1])});
        }
        {
            var Q0;
            Q0=qCreatedBy(makeId("Top.planeOp"),FACE);
            var sketch = newSketch(context, id + "F16", { "sketchPlane" : qUnion([Q0])});
            skCircle(sketch, "E44", {"center": v(-58.53, -50.7) * mm, "radius": 3.5 * mm});
            skCircle(sketch, "E45", {"center": v(-58.53, -50.7) * mm, "radius": 1.8 * mm});
            skSolve(sketch);
        }
        {
            var Q0;
            Q0=makeQuery(id+"F16.imprint","IMPRINT",FACE,{"disambiguationData":[TD([[makeQuery(id+"F16.imprint","IMPRINT",EDGE,{"derivedFrom":sQuery(id+"F16.wireOp",EDGE,"E44")}),1.0]])]});
            var Q1;
            Q1=makeQuery(id+"F16.imprint","IMPRINT",FACE,{"disambiguationData":[TD([[makeQuery(id+"F16.imprint","IMPRINT",EDGE,{"derivedFrom":sQuery(id+"F16.wireOp",EDGE,"E45")}),1.0]])]});
            extrude(context, id + "F17", {"entities" : qUnion([Q0, Q1]), "oppositeDirection" : true, "depth" : 2.4 * mm, "offsetDistance" : 25 * mm});
        }
        {
            var Q0;
            Q0=makeQuery(id+"F16.imprint","IMPRINT",FACE,{"disambiguationData":[TD([[makeQuery(id+"F16.imprint","IMPRINT",EDGE,{"derivedFrom":sQuery(id+"F16.wireOp",EDGE,"E45")}),1.0]])]});
            extrude(context, id + "F18", {"entities" : qUnion([Q0]), "operationType" : NewBodyOperationType.ADD, "depth" : 6 * mm, "offsetDistance" : 25 * mm, "hasDraft" : true, "draftAngle" : 3 * degree, "draftPullDirection" : true});
        }
        {
            var Q0;
            Q0=makeQuery(id+"F18.opExtrude","CAP_FACE",FACE,{"disambiguationData":[OSD([sQuery(id+"F16.wireOp",EDGE,"E45")])],"isStart":false});
            fillet(context, id + "F19", {"entities" : qUnion([Q0]), "radius" : 0.5 * mm, "tangentPropagation" : true, "allowEdgeOverflow" : false});
        }
        {
            var Q0;
            Q0=makeQuery(id+"F15.opPattern","COPY",BODY,{"derivedFrom":makeQuery(id+"F1.opExtrude","SWEPT_BODY",BODY,{"disambiguationData":[OSD([sQuery(id+"F0.wireOp",EDGE,"E0.bottom"),sQuery(id+"F0.wireOp",EDGE,"E0.top"),sQuery(id+"F0.wireOp",EDGE,"E0.left"),sQuery(id+"F0.wireOp",EDGE,"E0.right"),sQuery(id+"F0.wireOp",EDGE,"E2.bottom"),sQuery(id+"F0.wireOp",EDGE,"E2.top"),sQuery(id+"F0.wireOp",EDGE,"E2.left"),sQuery(id+"F0.wireOp",EDGE,"E2.right"),sQuery(id+"F0.wireOp",EDGE,"E3"),sQuery(id+"F0.wireOp",EDGE,"E4"),sQuery(id+"F0.wireOp",EDGE,"E5.bottom"),sQuery(id+"F0.wireOp",EDGE,"E5.top"),sQuery(id+"F0.wireOp",EDGE,"E5.left"),sQuery(id+"F0.wireOp",EDGE,"E5.right"),sQuery(id+"F0.wireOp",EDGE,"E6"),sQuery(id+"F0.wireOp",EDGE,"E7"),sQuery(id+"F0.wireOp",EDGE,"E8"),sQuery(id+"F0.wireOp",EDGE,"E9"),sQuery(id+"F0.wireOp",EDGE,"E10")])]}),"instanceName":"1"});
            transform(context, id + "F20", {"entities" : qUnion([Q0]), "transformType" : TransformType.TRANSLATION_3D, "dx" : 0 * mm, "dy" : -103.4 * mm, "dz" : 0 * mm, "makeCopy" : true});
        }
        {
            var Q0;
            Q0=makeQuery(id+"F20.opPattern","COPY",FACE,{"derivedFrom":makeQuery(id+"F15.opPattern","COPY",FACE,{"derivedFrom":makeQuery(id+"F11.opExtrude","SWEPT_FACE",FACE,{"disambiguationData":[OSD([sQuery(id+"F8.wireOp",EDGE,"E37.top")])]}),"instanceName":"1"}),"instanceName":"1"});
            var Q1;
            Q1=makeQuery(id+"F20.opPattern","COPY",FACE,{"derivedFrom":makeQuery(id+"F15.opPattern","COPY",FACE,{"derivedFrom":makeQuery(id+"F11.opExtrude","SWEPT_FACE",FACE,{"disambiguationData":[OSD([sQuery(id+"F8.wireOp",EDGE,"E36.top")])]}),"instanceName":"1"}),"instanceName":"1"});
            var Q2;
            Q2=makeQuery(id+"F20.opPattern","COPY",FACE,{"derivedFrom":makeQuery(id+"F15.opPattern","COPY",FACE,{"derivedFrom":makeQuery(id+"F10.opExtrude","SWEPT_FACE",FACE,{"disambiguationData":[OSD([sQuery(id+"F9.wireOp",EDGE,"E39.top")])]}),"instanceName":"1"}),"instanceName":"1"});
            var Q3;
            Q3=makeQuery(id+"F20.opPattern","COPY",FACE,{"derivedFrom":makeQuery(id+"F15.opPattern","COPY",FACE,{"derivedFrom":makeQuery(id+"F10.opExtrude","SWEPT_FACE",FACE,{"disambiguationData":[OSD([sQuery(id+"F9.wireOp",EDGE,"E38.top")])]}),"instanceName":"1"}),"instanceName":"1"});
            extrude(context, id + "F21", {"entities" : qUnion([Q0, Q1, Q2, Q3]), "operationType" : NewBodyOperationType.REMOVE, "endBound" : BoundingType.THROUGH_ALL, "oppositeDirection" : true, "depth" : 25 * mm, "offsetDistance" : 25 * mm});
        }
        {
            var Q0;
            Q0=makeQuery(id+"F20.opPattern","COPY",FACE,{"derivedFrom":makeQuery(id+"F15.opPattern","COPY",FACE,{"derivedFrom":makeQuery(id+"F2.opExtrude","CAP_FACE",FACE,{"disambiguationData":[OSD([sQuery(id+"F0.wireOp",EDGE,"E0.bottom"),sQuery(id+"F0.wireOp",EDGE,"E0.top"),sQuery(id+"F0.wireOp",EDGE,"E0.left"),sQuery(id+"F0.wireOp",EDGE,"E0.right"),sQuery(id+"F0.wireOp",EDGE,"E1.bottom"),sQuery(id+"F0.wireOp",EDGE,"E1.top"),sQuery(id+"F0.wireOp",EDGE,"E1.left"),sQuery(id+"F0.wireOp",EDGE,"E1.right")])],"isStart":false}),"instanceName":"1"}),"instanceName":"1"});
            extrude(context, id + "F22", {"entities" : qUnion([Q0]), "operationType" : NewBodyOperationType.ADD, "depth" : 6 * mm, "offsetDistance" : 25 * mm});
        }
        {
            var Q0;
            {var subQ0=sQuery(id+"F0.wireOp",EDGE,"E1.top");var subQ1=sQuery(id+"F9.wireOp",EDGE,"E39.top");var subQ2=sQuery(id+"F9.wireOp",EDGE,"E38.top");Q0=makeQuery(id+"F22.boolean.opBoolean","MERGE",FACE,{"derivedFrom":[makeQuery(id+"F21.boolean.opBoolean","MERGE",FACE,{"derivedFrom":[makeQuery(id+"F20.opPattern","COPY",FACE,{"derivedFrom":makeQuery(id+"F15.opPattern","COPY",FACE,{"derivedFrom":makeQuery(id+"F2.opExtrude","SWEPT_FACE",FACE,{"disambiguationData":[OSD([subQ0])]}),"instanceName":"1"}),"instanceName":"1"}),makeQuery(id+"F21.opExtrude","SWEPT_FACE",FACE,{"disambiguationData":[OSD([subQ2]),TDD([makeQuery(id+"F20.opPattern","COPY",EDGE,{"derivedFrom":makeQuery(id+"F15.opPattern","COPY",EDGE,{"derivedFrom":makeQuery(id+"F10.opExtrude","CAP_EDGE",EDGE,{"disambiguationData":[OSD([subQ2])],"isStart":true}),"instanceName":"1"}),"instanceName":"1"})])]}),makeQuery(id+"F21.opExtrude","SWEPT_FACE",FACE,{"disambiguationData":[OSD([subQ1]),TDD([makeQuery(id+"F20.opPattern","COPY",EDGE,{"derivedFrom":makeQuery(id+"F15.opPattern","COPY",EDGE,{"derivedFrom":makeQuery(id+"F10.opExtrude","CAP_EDGE",EDGE,{"disambiguationData":[OSD([subQ1])],"isStart":true}),"instanceName":"1"}),"instanceName":"1"})])]})]}),makeQuery(id+"F22.opExtrude","SWEPT_FACE",FACE,{"disambiguationData":[OSD([subQ0])]})]});}
            var sketch = newSketch(context, id + "F23", { "sketchPlane" : qUnion([Q0])});
            skLineSegment(sketch, "E46.bottom", {"start": v(79.26, 26) * mm, "end": v(99.26, 26) * mm});
            skLineSegment(sketch, "E46.top", {"start": v(79.26, 22) * mm, "end": v(99.26, 22) * mm});
            skLineSegment(sketch, "E46.left", {"start": v(99.26, 22) * mm, "end": v(99.26, 26) * mm});
            skLineSegment(sketch, "E46.right", {"start": v(79.26, 22) * mm, "end": v(79.26, 26) * mm});
            skLineSegment(sketch, "E47.bottom", {"start": v(49.26, 26) * mm, "end": v(29.26, 26) * mm});
            skLineSegment(sketch, "E47.top", {"start": v(49.26, 22) * mm, "end": v(29.26, 22) * mm});
            skLineSegment(sketch, "E47.left", {"start": v(49.26, 22) * mm, "end": v(49.26, 26) * mm});
            skLineSegment(sketch, "E47.right", {"start": v(29.26, 22) * mm, "end": v(29.26, 26) * mm});
            skSolve(sketch);
        }
        {
            var Q0;
            Q0=makeQuery(id+"F23.imprint","IMPRINT",FACE,{"disambiguationData":[TD([[makeQuery(id+"F23.imprint","IMPRINT",EDGE,{"derivedFrom":sQuery(id+"F23.wireOp",EDGE,"E47.bottom")}),1.0]])]});
            var Q1;
            Q1=makeQuery(id+"F23.imprint","IMPRINT",FACE,{"disambiguationData":[TD([[makeQuery(id+"F23.imprint","IMPRINT",EDGE,{"derivedFrom":sQuery(id+"F23.wireOp",EDGE,"E46.bottom")}),1.0]])]});
            extrude(context, id + "F24", {"entities" : qUnion([Q0, Q1]), "operationType" : NewBodyOperationType.ADD, "depth" : 20 * mm, "offsetDistance" : 25 * mm});
        }
        {
            var Q0;
            Q0=makeQuery(id+"F24.opExtrude","SWEPT_FACE",FACE,{"disambiguationData":[OSD([sQuery(id+"F23.wireOp",EDGE,"E47.bottom")])]});
            var sketch = newSketch(context, id + "F25", { "sketchPlane" : qUnion([Q0])});
            skCircle(sketch, "E48", {"center": v(39.26, -110.77) * mm, "radius": 2.1 * mm});
            skPoint(sketch, "E48.centerSnap0", {"position": v(49.26, -110.77) * mm});
            skPoint(sketch, "E48.centerSnap1", {"position": v(39.26, -120.77) * mm});
            skCircle(sketch, "E49", {"center": v(89.26, -110.77) * mm, "radius": 2.1 * mm});
            skSolve(sketch);
        }
        {
            var Q0;
            Q0=makeQuery(id+"F25.imprint","IMPRINT",FACE,{"disambiguationData":[TD([[makeQuery(id+"F25.imprint","IMPRINT",EDGE,{"derivedFrom":sQuery(id+"F25.wireOp",EDGE,"E48")}),1.0]])]});
            var Q1;
            Q1=makeQuery(id+"F25.imprint","IMPRINT",FACE,{"disambiguationData":[TD([[makeQuery(id+"F25.imprint","IMPRINT",EDGE,{"derivedFrom":sQuery(id+"F25.wireOp",EDGE,"E49")}),1.0]])]});
            extrude(context, id + "F26", {"entities" : qUnion([Q0, Q1]), "operationType" : NewBodyOperationType.REMOVE, "endBound" : BoundingType.THROUGH_ALL, "oppositeDirection" : true, "depth" : 25 * mm, "offsetDistance" : 25 * mm});
        }
        {
            var Q0;
            Q0=makeQuery(id+"F24.opExtrude","CAP_EDGE",EDGE,{"disambiguationData":[OSD([sQuery(id+"F23.wireOp",EDGE,"E46.right")])],"isStart":false});
            var Q1;
            Q1=makeQuery(id+"F24.opExtrude","CAP_EDGE",EDGE,{"disambiguationData":[OSD([sQuery(id+"F23.wireOp",EDGE,"E47.left")])],"isStart":false});
            var Q2;
            Q2=makeQuery(id+"F24.opExtrude","CAP_EDGE",EDGE,{"disambiguationData":[OSD([sQuery(id+"F23.wireOp",EDGE,"E47.right")])],"isStart":false});
            var Q3;
            Q3=makeQuery(id+"F24.opExtrude","CAP_EDGE",EDGE,{"disambiguationData":[OSD([sQuery(id+"F23.wireOp",EDGE,"E46.left")])],"isStart":false});
            fillet(context, id + "F27", {"entities" : qUnion([Q0, Q1, Q2, Q3]), "radius" : 5 * mm, "tangentPropagation" : true, "allowEdgeOverflow" : false});
        }
    });
